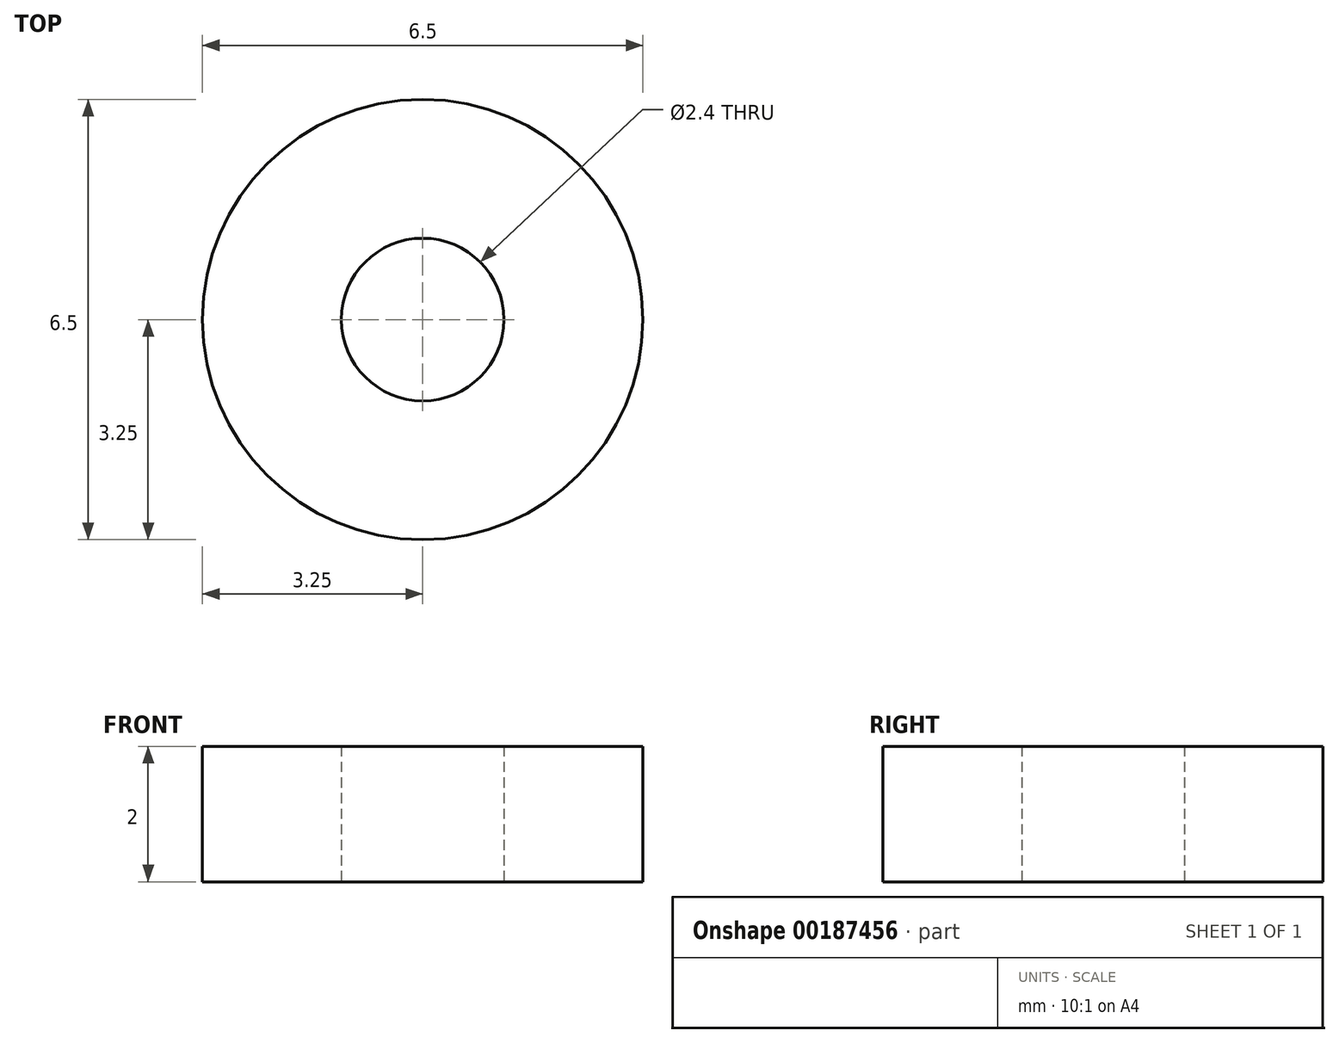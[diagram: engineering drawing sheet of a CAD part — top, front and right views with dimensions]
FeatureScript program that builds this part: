
annotation { "Feature Type Name" : "Feature", "Feature Type Description" : "" }
export const myFeature = defineFeature(function(context is Context, id is Id, definition is map)
    precondition{}
    {
        {
            var Q0;
            Q0=qCreatedBy(makeId("Top.planeOp"),FACE);
            var sketch = newSketch(context, id + "F0", { "sketchPlane" : qUnion([Q0])});
            skCircle(sketch, "E0", {"center": v(0, 0) * mm, "radius": 3.25 * mm});
            skSolve(sketch);
        }
        {
            var Q0;
            Q0=makeQuery(id+"F0.imprint","IMPRINT",FACE,{"disambiguationData":[TD([[makeQuery(id+"F0.imprint","IMPRINT",EDGE,{"derivedFrom":sQuery(id+"F0.wireOp",EDGE,"E0")}),1.0]])]});
            var Q1;
            Q1=sQuery(id+"F0.wireOp",EDGE,"E0");
            extrude(context, id + "F1", {"entities" : qUnion([Q0]), "surfaceEntities" : qUnion([Q1]), "depth" : 2 * mm});
        }
        {
            var Q0;
            Q0=qCreatedBy(makeId("Top.planeOp"),FACE);
            var sketch = newSketch(context, id + "F2", { "sketchPlane" : qUnion([Q0])});
            skCircle(sketch, "E1", {"center": v(0, 0) * mm, "radius": 0.35 * mm});
            skSolve(sketch);
        }
        {
            var Q0;
            Q0=sQuery(id+"F2.wireOp",VERTEX,"E1.center");
            var Q1;
            Q1=makeQuery(id+"F1.opExtrude","SWEPT_BODY",BODY,{"disambiguationData":[OSD([sQuery(id+"F0.wireOp",EDGE,"E0")])]});
            hole(context, id + "F3", {"style" : HoleStyle.SIMPLE, "endStyle" : HoleEndStyle.THROUGH, "oppositeDirection" : true, "holeDiameter" : 2.4 * mm, "locations" : qUnion([Q0]), "scope" : qUnion([Q1]), "isTappedThrough" : true});
        }
    });
